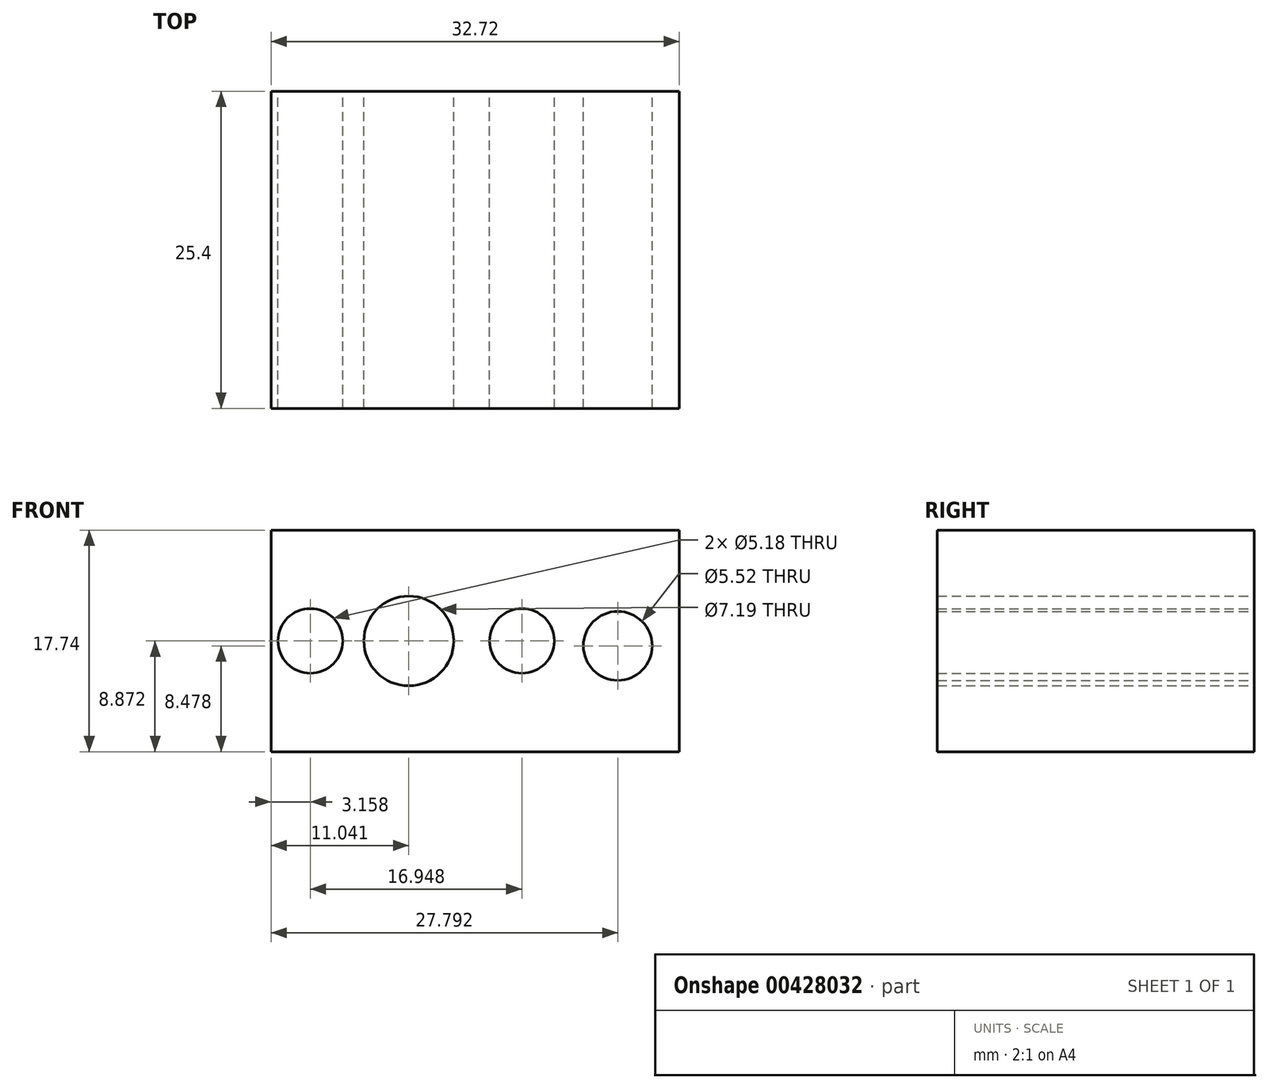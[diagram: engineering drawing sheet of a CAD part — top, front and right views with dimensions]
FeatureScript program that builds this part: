
annotation { "Feature Type Name" : "Feature", "Feature Type Description" : "" }
export const myFeature = defineFeature(function(context is Context, id is Id, definition is map)
    precondition{}
    {
        {
            var Q0;
            Q0=qCreatedBy(makeId("Front.planeOp"),FACE);
            var sketch = newSketch(context, id + "F0", { "sketchPlane" : qUnion([Q0])});
            skLineSegment(sketch, "E0", {"start": v(-51.44, -30.55) * mm, "end": v(-51.44, -12.8) * mm});
            skLineSegment(sketch, "E1", {"start": v(-51.44, -12.8) * mm, "end": v(-18.72, -12.8) * mm});
            skLineSegment(sketch, "E2", {"start": v(-18.72, -12.8) * mm, "end": v(-18.72, -30.55) * mm});
            skLineSegment(sketch, "E3", {"start": v(-18.72, -30.55) * mm, "end": v(-51.44, -30.55) * mm});
            skCircle(sketch, "E4", {"center": v(-40.4, -21.68) * mm, "radius": 3.6 * mm});
            skCircle(sketch, "E5", {"center": v(-31.33, -21.68) * mm, "radius": 2.6 * mm});
            skCircle(sketch, "E6", {"center": v(-23.65, -22.07) * mm, "radius": 2.76 * mm});
            skCircle(sketch, "E7", {"center": v(-48.28, -21.68) * mm, "radius": 2.6 * mm});
            skSolve(sketch);
        }
        {
            var Q0;
            Q0 = qSketchRegion(id + "F0", true);
            extrude(context, id + "F1", {"entities" : qUnion([Q0]), "depth" : 25.4 * mm, "offsetDistance" : 25.4 * mm});
        }
    });
